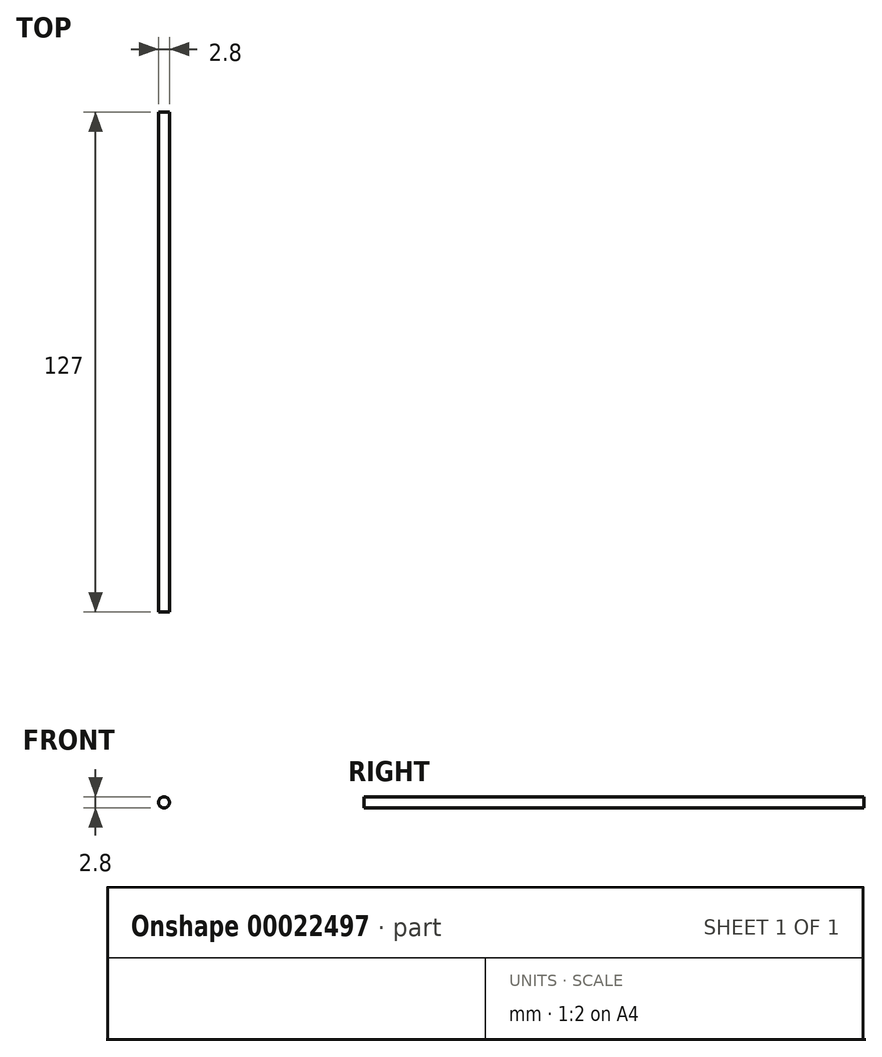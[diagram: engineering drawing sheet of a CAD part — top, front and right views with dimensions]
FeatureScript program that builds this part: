
annotation { "Feature Type Name" : "Feature", "Feature Type Description" : "" }
export const myFeature = defineFeature(function(context is Context, id is Id, definition is map)
    precondition{}
    {
        {
            var Q0;
            Q0=qCreatedBy(makeId("Front.planeOp"),FACE);
            var sketch = newSketch(context, id + "F0", { "sketchPlane" : qUnion([Q0])});
            skCircle(sketch, "E0", {"center": v(0, 0) * mm, "radius": 1.4 * mm});
            skSolve(sketch);
        }
        {
            var Q0;
            Q0=makeQuery(id+"F0.imprint","IMPRINT",FACE,{"disambiguationData":[TD([[makeQuery(id+"F0.imprint","IMPRINT",EDGE,{"derivedFrom":sQuery(id+"F0.wireOp",EDGE,"E0")}),1.0]])]});
            extrude(context, id + "F1", {"entities" : qUnion([Q0]), "depth" : 127 * mm});
        }
    });
